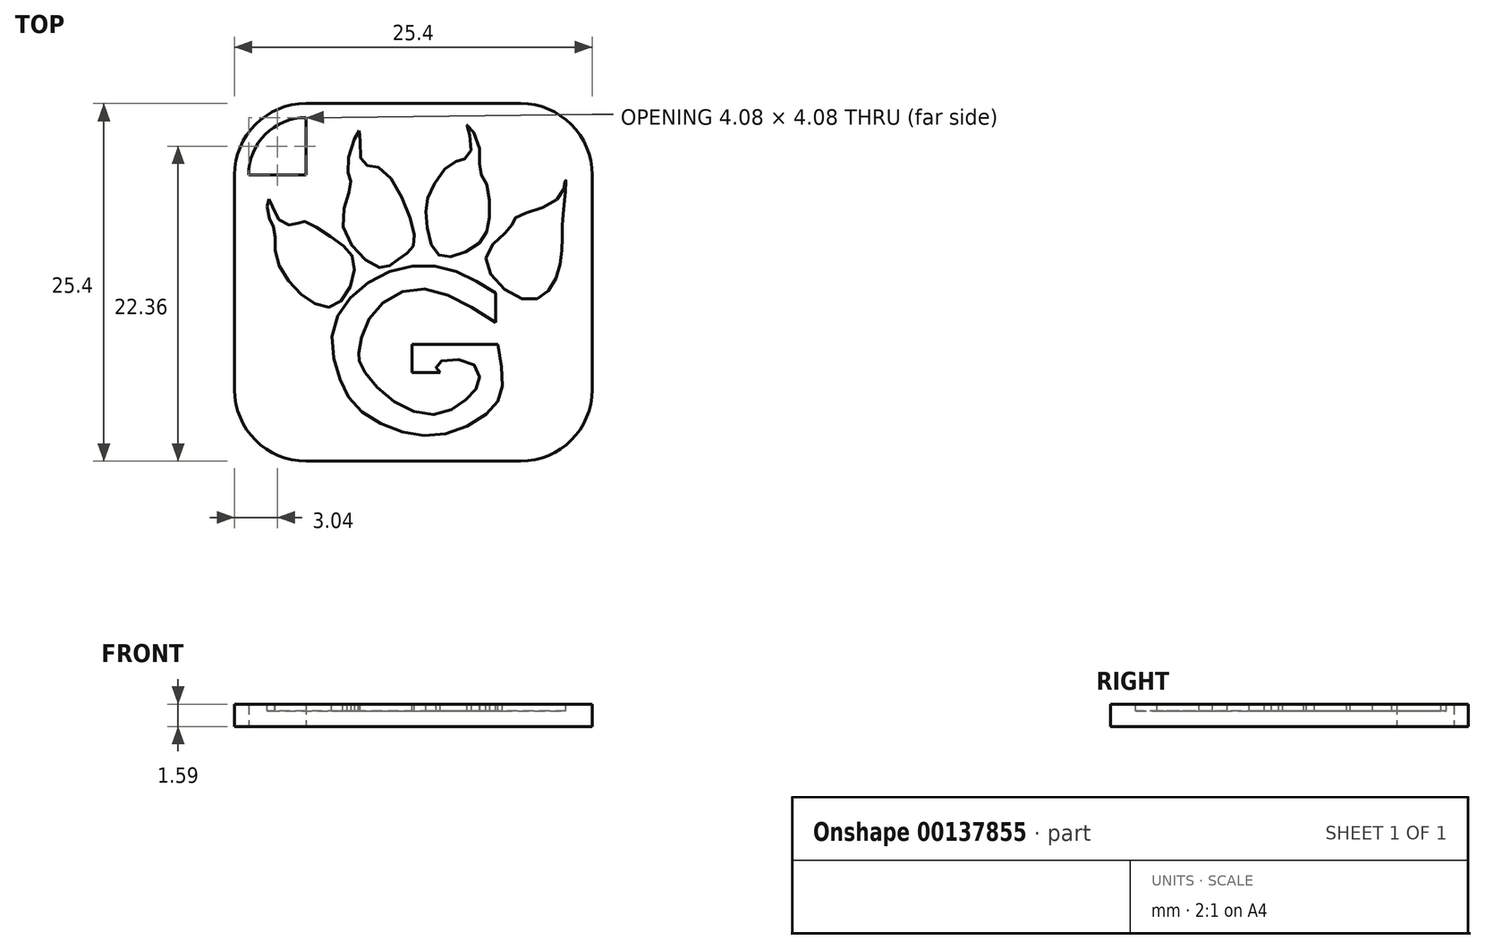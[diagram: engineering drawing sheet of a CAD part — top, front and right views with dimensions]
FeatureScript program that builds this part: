
annotation { "Feature Type Name" : "Feature", "Feature Type Description" : "" }
export const myFeature = defineFeature(function(context is Context, id is Id, definition is map)
    precondition{}
    {
        {
            var Q0;
            Q0=qCreatedBy(makeId("Top.planeOp"),FACE);
            var sketch = newSketch(context, id + "F0", { "sketchPlane" : qUnion([Q0])});
            skLineSegment(sketch, "E0.bottom", {"start": v(5.08, 0) * mm, "end": v(20.32, 0) * mm});
            skLineSegment(sketch, "E0.top", {"start": v(5.08, -25.4) * mm, "end": v(20.32, -25.4) * mm});
            skLineSegment(sketch, "E0.left", {"start": v(0, -5.08) * mm, "end": v(0, -20.32) * mm});
            skLineSegment(sketch, "E0.right", {"start": v(25.4, -5.08) * mm, "end": v(25.4, -20.32) * mm});
            skPoint(sketch, "E1.visualSharp", {"position": v(0, 0) * mm});
            skArc(sketch, "E1.filletArc", {"start": v(5.08, 0) * mm, "mid": v(1.49, -1.49) * mm, "end": v(0, -5.08) * mm});
            skPoint(sketch, "E2.visualSharp", {"position": v(25.4, 0) * mm});
            skArc(sketch, "E2.filletArc", {"start": v(25.4, -5.08) * mm, "mid": v(23.91, -1.49) * mm, "end": v(20.32, 0) * mm});
            skPoint(sketch, "E3.visualSharp", {"position": v(25.4, -25.4) * mm});
            skArc(sketch, "E3.filletArc", {"start": v(20.32, -25.4) * mm, "mid": v(23.91, -23.91) * mm, "end": v(25.4, -20.32) * mm});
            skPoint(sketch, "E4.visualSharp", {"position": v(0, -25.4) * mm});
            skArc(sketch, "E4.filletArc", {"start": v(0, -20.32) * mm, "mid": v(1.49, -23.91) * mm, "end": v(5.08, -25.4) * mm});
            skLineSegment(sketch, "E5.0", {"start": v(8.16, -5.08) * mm, "end": v(8.16, -5.08) * mm});
            skArc(sketch, "E6", {"start": v(5.08, -1) * mm, "mid": v(2.2, -2.2) * mm, "end": v(1, -5.08) * mm});
            skLineSegment(sketch, "E7", {"start": v(5.08, -5.08) * mm, "end": v(5.08, -1) * mm});
            skLineSegment(sketch, "E8", {"start": v(5.08, -5.08) * mm, "end": v(1, -5.08) * mm});
            skSolve(sketch);
        }
        {
            var Q0;
            Q0=makeQuery(id+"F0.imprint","IMPRINT",FACE,{"disambiguationData":[TD([[makeQuery(id+"F0.imprint","IMPRINT",EDGE,{"derivedFrom":sQuery(id+"F0.wireOp",EDGE,"E0.bottom")}),-1.0]])]});
            extrude(context, id + "F1", {"entities" : qUnion([Q0]), "depth" : 1.59 * mm});
        }
        {
            var Q0;
            Q0=makeQuery(id+"F1.opExtrude","CAP_FACE",FACE,{"disambiguationData":[OSD([sQuery(id+"F0.wireOp",EDGE,"E0.bottom"),sQuery(id+"F0.wireOp",EDGE,"E0.top"),sQuery(id+"F0.wireOp",EDGE,"E0.left"),sQuery(id+"F0.wireOp",EDGE,"E0.right")])],"isStart":false});
            var sketch = newSketch(context, id + "F2", { "sketchPlane" : qUnion([Q0])});
            skPoint(sketch, "E9", {"position": v(-22.86, 0) * mm});
            skFitSpline(sketch, "E10", {"points": [v(2.45, -6.77) * mm, v(3.1, -8.19) * mm, v(4.34, -8.58) * mm, v(4.9, -8.38) * mm, v(7.19, -9.7) * mm, v(8.52, -11.35) * mm, v(7.28, -14.27) * mm, v(5.06, -13.81) * mm, v(2.96, -10.9) * mm, v(2.83, -8.93) * mm, v(2.37, -7.83) * mm, v(2.45, -6.77) * mm]});
            skFitSpline(sketch, "E11", {"points": [v(8.86, -1.92) * mm, v(9.04, -4.13) * mm, v(10.33, -4.6) * mm, v(12.67, -8.84) * mm, v(12.54, -10.35) * mm, v(11.5, -11.16) * mm, v(10.3, -11.65) * mm, v(7.71, -8.69) * mm, v(8.27, -5.66) * mm, v(8.01, -4.53) * mm, v(8.86, -1.92) * mm]});
            skFitSpline(sketch, "E12", {"points": [v(15.35, -10.89) * mm, v(14.2, -10.48) * mm, v(13.6, -8.04) * mm, v(13.88, -6.29) * mm, v(15.44, -4.23) * mm, v(16.34, -3.94) * mm, v(16.82, -2.94) * mm, v(16.52, -1.54) * mm, v(17.33, -2.8) * mm, v(17.42, -4.78) * mm, v(17.91, -5.75) * mm, v(18.07, -8.24) * mm, v(17.45, -9.84) * mm, v(15.35, -10.89) * mm]});
            skFitSpline(sketch, "E13", {"points": [v(17.83, -10.98) * mm, v(20.7, -13.94) * mm, v(22.7, -12.7) * mm, v(23.26, -10.16) * mm, v(23.33, -7.9) * mm, v(23.51, -5.42) * mm, v(23.48, -5.42) * mm, v(23.46, -5.6) * mm, v(22.77, -6.91) * mm, v(19.95, -8.1) * mm, v(19.65, -8.74) * mm, v(17.83, -10.98) * mm]});
            skLineSegment(sketch, "E14", {"start": v(12.6, -17.12) * mm, "end": v(18.71, -17.12) * mm});
            skLineSegment(sketch, "E15", {"start": v(12.6, -17.12) * mm, "end": v(12.6, -19.1) * mm});
            skLineSegment(sketch, "E16", {"start": v(12.6, -19.1) * mm, "end": v(14.6, -19.1) * mm});
            skFitSpline(sketch, "E17", {"points": [v(14.6, -19.1) * mm, v(14.35, -18.84) * mm, v(14.44, -18.42) * mm, v(16.75, -18.39) * mm, v(17.38, -19.65) * mm, v(16.45, -21.01) * mm, v(13.9, -22.1) * mm, v(10.34, -20.37) * mm, v(8.88, -18.35) * mm, v(8.83, -17.75) * mm, v(9.63, -15.16) * mm, v(13.15, -13.16) * mm, v(18.55, -15.56) * mm], "startDerivative": vector(-8.65, 6.33) * mm, "endDerivative": vector(39.26, -25.86) * mm});
            skLineSegment(sketch, "E18", {"start": v(18.55, -15.56) * mm, "end": v(18.55, -13.47) * mm});
            skFitSpline(sketch, "E19", {"points": [v(18.55, -13.47) * mm, v(15.41, -11.82) * mm, v(11.98, -11.65) * mm, v(8.56, -13.47) * mm, v(6.94, -16.3) * mm, v(7.48, -19.55) * mm, v(8.95, -21.82) * mm, v(12.16, -23.38) * mm, v(15.35, -23.37) * mm, v(18.3, -21.66) * mm, v(19, -20.12) * mm, v(18.71, -17.12) * mm], "startDerivative": vector(-31.6, 20.05) * mm, "endDerivative": vector(-6.01, 36.91) * mm});
            skSolve(sketch);
        }
        {
            var Q0;
            Q0 = qSketchRegion(id + "F2", true);
            extrude(context, id + "F3", {"entities" : qUnion([Q0]), "operationType" : NewBodyOperationType.REMOVE, "oppositeDirection" : true, "depth" : 0.5 * mm});
        }
    });
